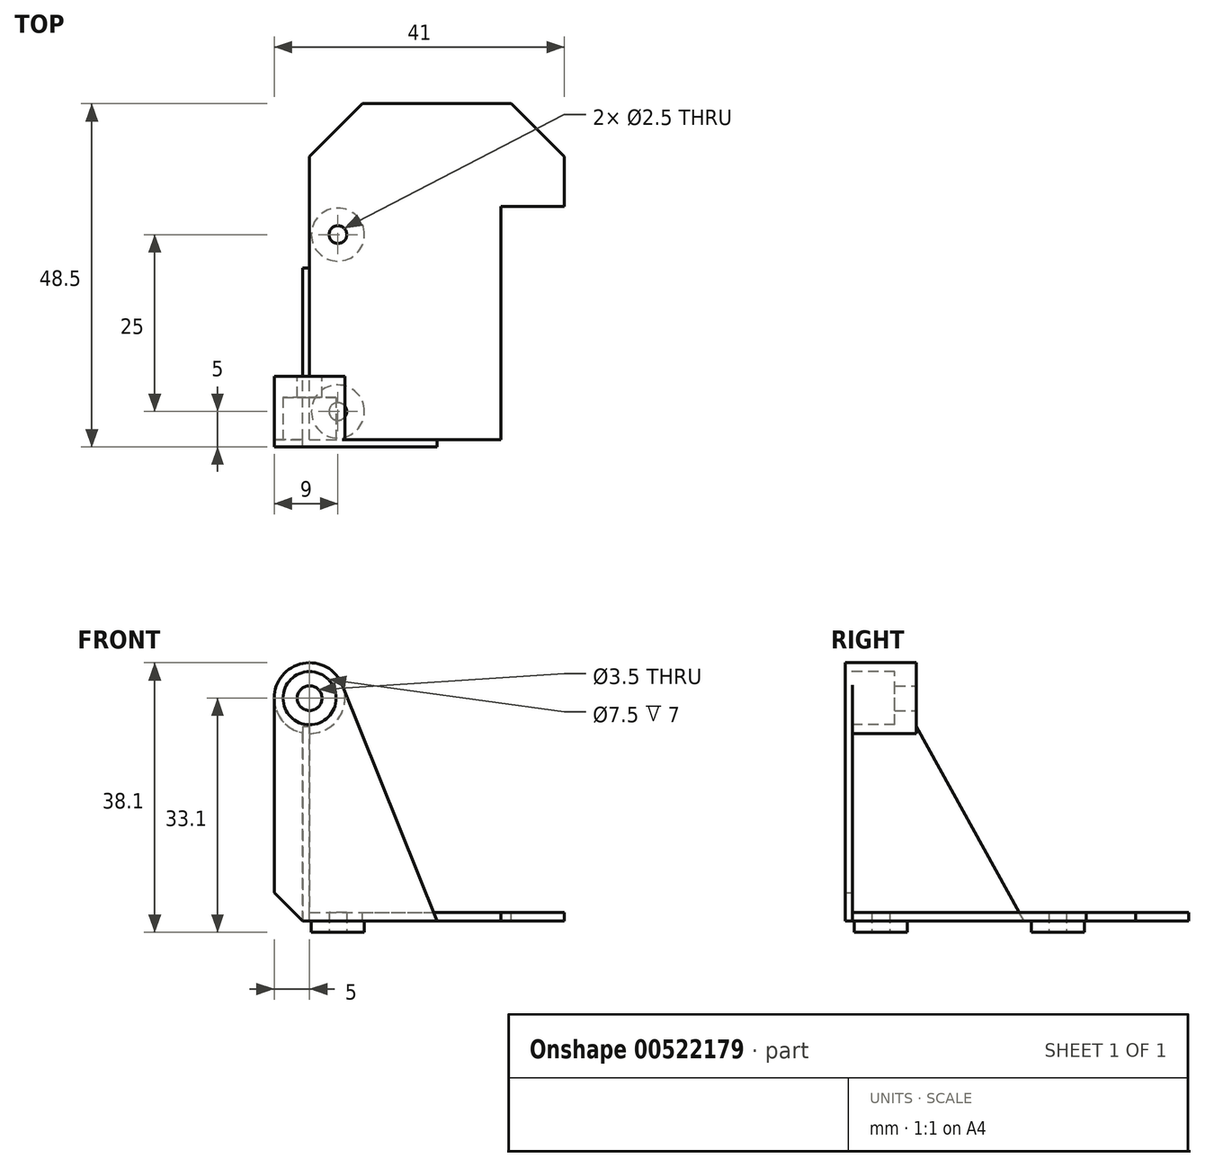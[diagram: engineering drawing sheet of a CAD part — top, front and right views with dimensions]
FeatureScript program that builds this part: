
annotation { "Feature Type Name" : "Feature", "Feature Type Description" : "" }
export const myFeature = defineFeature(function(context is Context, id is Id, definition is map)
    precondition{}
    {
        {
            var Q0;
            Q0=qCreatedBy(makeId("Top.planeOp"),FACE);
            var sketch = newSketch(context, id + "F0", { "sketchPlane" : qUnion([Q0])});
            skLineSegment(sketch, "E0.bottom", {"start": v(0, 0) * mm, "end": v(36, 0) * mm});
            skLineSegment(sketch, "E0.top", {"start": v(0, 48.5) * mm, "end": v(36, 48.5) * mm});
            skLineSegment(sketch, "E0.left", {"start": v(0, 0) * mm, "end": v(0, 48.5) * mm});
            skLineSegment(sketch, "E0.right", {"start": v(36, 0) * mm, "end": v(36, 48.5) * mm});
            skLineSegment(sketch, "E1.bottom", {"start": v(0, 20) * mm, "end": v(-1, 20) * mm});
            skLineSegment(sketch, "E1.top", {"start": v(0, -2) * mm, "end": v(-1, -2) * mm});
            skLineSegment(sketch, "E1.left", {"start": v(0, 20) * mm, "end": v(0, 0) * mm});
            skLineSegment(sketch, "E1.right", {"start": v(-1, 20) * mm, "end": v(-1, -2) * mm});
            skLineSegment(sketch, "E2.bottom", {"start": v(36, 0) * mm, "end": v(0, 0) * mm});
            skLineSegment(sketch, "E2.top", {"start": v(36, -2) * mm, "end": v(0, -2) * mm});
            skLineSegment(sketch, "E2.left", {"start": v(36, 0) * mm, "end": v(36, -2) * mm});
            skCircle(sketch, "E3", {"center": v(4, 4) * mm, "radius": 1.25 * mm});
            skCircle(sketch, "E4", {"center": v(4, 29) * mm, "radius": 1.25 * mm});
            skSolve(sketch);
        }
        {
            var Q0;
            Q0=makeQuery(id+"F0.imprint","IMPRINT",FACE,{"disambiguationData":[TD([[makeQuery(id+"F0.imprint","IMPRINT",EDGE,{"derivedFrom":sQuery(id+"F0.wireOp",EDGE,"E0.top")}),-1.0]])]});
            extrude(context, id + "F1", {"entities" : qUnion([Q0]), "depth" : 1.2 * mm, "offsetDistance" : 25 * mm});
        }
        {
            var Q0;
            Q0=makeQuery(id+"F0.imprint","IMPRINT",FACE,{"disambiguationData":[TD([[makeQuery(id+"F0.imprint","IMPRINT",EDGE,{"derivedFrom":sQuery(id+"F0.wireOp",EDGE,"E0.top")}),-1.0]])]});
            var sketch = newSketch(context, id + "F2", { "sketchPlane" : qUnion([Q0])});
            skCircle(sketch, "E5", {"center": v(4, 29) * mm, "radius": 3.75 * mm});
            skCircle(sketch, "E6", {"center": v(4, 29) * mm, "radius": 1.25 * mm});
            skCircle(sketch, "E7", {"center": v(4, 4) * mm, "radius": 3.75 * mm});
            skCircle(sketch, "E8", {"center": v(4, 4) * mm, "radius": 1.25 * mm});
            skSolve(sketch);
        }
        {
            var Q0;
            Q0 = qSketchRegion(id + "F2", true);
            extrude(context, id + "F3", {"entities" : qUnion([Q0]), "operationType" : NewBodyOperationType.ADD, "oppositeDirection" : true, "depth" : 1.6 * mm, "offsetDistance" : 25 * mm});
        }
        {
            var Q0;
            Q0=qCreatedBy(makeId("Front.planeOp"),FACE);
            var sketch = newSketch(context, id + "F4", { "sketchPlane" : qUnion([Q0])});
            skCircle(sketch, "E9", {"center": v(0, 31.5) * mm, "radius": 1.75 * mm});
            skCircle(sketch, "E10", {"center": v(0, 31.5) * mm, "radius": 5 * mm});
            skLineSegment(sketch, "E11", {"start": v(-5, 31.5) * mm, "end": v(-5, 0) * mm});
            skLineSegment(sketch, "E12", {"start": v(0, 0) * mm, "end": v(-5, 0) * mm});
            skLineSegment(sketch, "E13", {"start": v(4.64, 33.36) * mm, "end": v(18, 0) * mm});
            skLineSegment(sketch, "E14", {"start": v(18, 0) * mm, "end": v(0, 0) * mm});
            skLineSegment(sketch, "E15", {"start": v(0, 0) * mm, "end": v(0, 31.5) * mm, "construction": true});
            skSolve(sketch);
        }
        {
            var Q0;
            {var subQ1=sQuery(id+"F4.wireOp",EDGE,"E11");Q0=makeQuery(id+"F4.imprint","IMPRINT",FACE,{"disambiguationData":[TD([[makeQuery(id+"F4.imprint","IMPRINT",EDGE,{"derivedFrom":subQ1}),1.0]])]});}
            var Q1;
            Q1=makeQuery(id+"F4.imprint","IMPRINT",FACE,{"disambiguationData":[TD([[makeQuery(id+"F4.imprint","IMPRINT",EDGE,{"derivedFrom":sQuery(id+"F4.wireOp",EDGE,"E9")}),-1.0]])]});
            extrude(context, id + "F5", {"entities" : qUnion([Q0, Q1]), "operationType" : NewBodyOperationType.ADD, "depth" : 1 * mm, "offsetDistance" : 25 * mm});
        }
        {
            var Q0;
            Q0=makeQuery(id+"F4.imprint","IMPRINT",FACE,{"disambiguationData":[TD([[makeQuery(id+"F4.imprint","IMPRINT",EDGE,{"derivedFrom":sQuery(id+"F4.wireOp",EDGE,"E9")}),-1.0]])]});
            extrude(context, id + "F6", {"entities" : qUnion([Q0]), "operationType" : NewBodyOperationType.ADD, "oppositeDirection" : true, "depth" : 9 * mm, "offsetDistance" : 25 * mm});
        }
        {
            var Q0;
            Q0=makeQuery(id+"F1.opExtrude","SWEPT_FACE",FACE,{"disambiguationData":[OSD([sQuery(id+"F0.wireOp",EDGE,"E0.left"),sQuery(id+"F0.wireOp",EDGE,"E1.left")])]});
            var sketch = newSketch(context, id + "F7", { "sketchPlane" : qUnion([Q0])});
            skLineSegment(sketch, "E16", {"start": v(-24.25, 0) * mm, "end": v(-9, 27.5) * mm});
            skLineSegment(sketch, "E17", {"start": v(0, 27.5) * mm, "end": v(0, 0) * mm});
            skLineSegment(sketch, "E18", {"start": v(0, 0) * mm, "end": v(-24.25, 0) * mm});
            skLineSegment(sketch, "E19", {"start": v(0, 27.5) * mm, "end": v(-9, 27.5) * mm});
            skPoint(sketch, "E20", {"position": v(0, 26.5) * mm});
            skSolve(sketch);
        }
        {
            var Q0;
            Q0 = qSketchRegion(id + "F7", true);
            extrude(context, id + "F8", {"entities" : qUnion([Q0]), "operationType" : NewBodyOperationType.ADD, "depth" : 1 * mm, "offsetDistance" : 25 * mm});
        }
        {
            var Q0;
            {var subQ1=sQuery(id+"F4.wireOp",EDGE,"E11");Q0=makeQuery(id+"F4.imprint","IMPRINT",FACE,{"disambiguationData":[TD([[makeQuery(id+"F4.imprint","IMPRINT",EDGE,{"derivedFrom":subQ1}),1.0]])]});}
            var sketch = newSketch(context, id + "F9", { "sketchPlane" : qUnion([Q0])});
            skLineSegment(sketch, "E21", {"start": v(-1, 0) * mm, "end": v(-5, 4) * mm});
            skLineSegment(sketch, "E22", {"start": v(-5, 4) * mm, "end": v(-5, 0) * mm});
            skLineSegment(sketch, "E23", {"start": v(-5, 0) * mm, "end": v(-1, 0) * mm});
            skSolve(sketch);
        }
        {
            var Q0;
            Q0 = qSketchRegion(id + "F9", true);
            extrude(context, id + "F10", {"entities" : qUnion([Q0]), "operationType" : NewBodyOperationType.REMOVE, "endBound" : BoundingType.THROUGH_ALL, "depth" : 25 * mm, "offsetDistance" : 25 * mm});
        }
        {
            var Q0;
            Q0=makeQuery(id+"F5.opExtrude","CAP_FACE",FACE,{"disambiguationData":[OSD([sQuery(id+"F4.wireOp",EDGE,"E9"),sQuery(id+"F4.wireOp",EDGE,"E10"),sQuery(id+"F4.wireOp",EDGE,"E11"),sQuery(id+"F4.wireOp",EDGE,"E12"),sQuery(id+"F4.wireOp",EDGE,"E13"),sQuery(id+"F4.wireOp",EDGE,"E14")])],"isStart":false});
            var sketch = newSketch(context, id + "F11", { "sketchPlane" : qUnion([Q0])});
            skCircle(sketch, "E24", {"center": v(0, 31.5) * mm, "radius": 3.75 * mm});
            skSolve(sketch);
        }
        {
            var Q0;
            Q0 = qSketchRegion(id + "F11", true);
            extrude(context, id + "F12", {"entities" : qUnion([Q0]), "operationType" : NewBodyOperationType.REMOVE, "oppositeDirection" : true, "depth" : 7 * mm, "offsetDistance" : 25 * mm});
        }
        {
            var Q0;
            Q0=makeQuery(id+"F1.opExtrude","CAP_FACE",FACE,{"disambiguationData":[OSD([sQuery(id+"F0.wireOp",EDGE,"E0.top"),sQuery(id+"F0.wireOp",EDGE,"E0.left"),sQuery(id+"F0.wireOp",EDGE,"E0.right"),sQuery(id+"F0.wireOp",EDGE,"E1.left"),sQuery(id+"F0.wireOp",EDGE,"E2.bottom"),sQuery(id+"F0.wireOp",EDGE,"E3"),sQuery(id+"F0.wireOp",EDGE,"E4")])],"isStart":false});
            var sketch = newSketch(context, id + "F13", { "sketchPlane" : qUnion([Q0])});
            skLineSegment(sketch, "E25.bottom", {"start": v(0, 48.5) * mm, "end": v(36, 48.5) * mm});
            skLineSegment(sketch, "E25.top", {"start": v(7.49, 47.5) * mm, "end": v(28.51, 47.5) * mm});
            skLineSegment(sketch, "E25.left", {"start": v(0, 48.5) * mm, "end": v(0, 47.5) * mm});
            skLineSegment(sketch, "E25.right", {"start": v(36, 48.5) * mm, "end": v(36, 47.5) * mm});
            skLineSegment(sketch, "E26.bottom", {"start": v(36, 0) * mm, "end": v(27, 0) * mm});
            skLineSegment(sketch, "E26.top", {"start": v(36, 33) * mm, "end": v(27, 33) * mm});
            skLineSegment(sketch, "E26.left", {"start": v(36, 0) * mm, "end": v(36, 33) * mm});
            skLineSegment(sketch, "E26.right", {"start": v(27, 0) * mm, "end": v(27, 33) * mm});
            skLineSegment(sketch, "E27", {"start": v(0, 40.01) * mm, "end": v(7.49, 47.5) * mm});
            skLineSegment(sketch, "E28", {"start": v(0, 40.01) * mm, "end": v(0, 47.5) * mm});
            skLineSegment(sketch, "E29", {"start": v(28.51, 47.5) * mm, "end": v(36, 40.01) * mm});
            skLineSegment(sketch, "E30", {"start": v(36, 40.01) * mm, "end": v(36, 47.5) * mm});
            skSolve(sketch);
        }
        {
            var Q0;
            Q0 = qSketchRegion(id + "F13", true);
            extrude(context, id + "F14", {"entities" : qUnion([Q0]), "operationType" : NewBodyOperationType.REMOVE, "endBound" : BoundingType.THROUGH_ALL, "oppositeDirection" : true, "depth" : 25 * mm, "offsetDistance" : 25 * mm});
        }
    });
